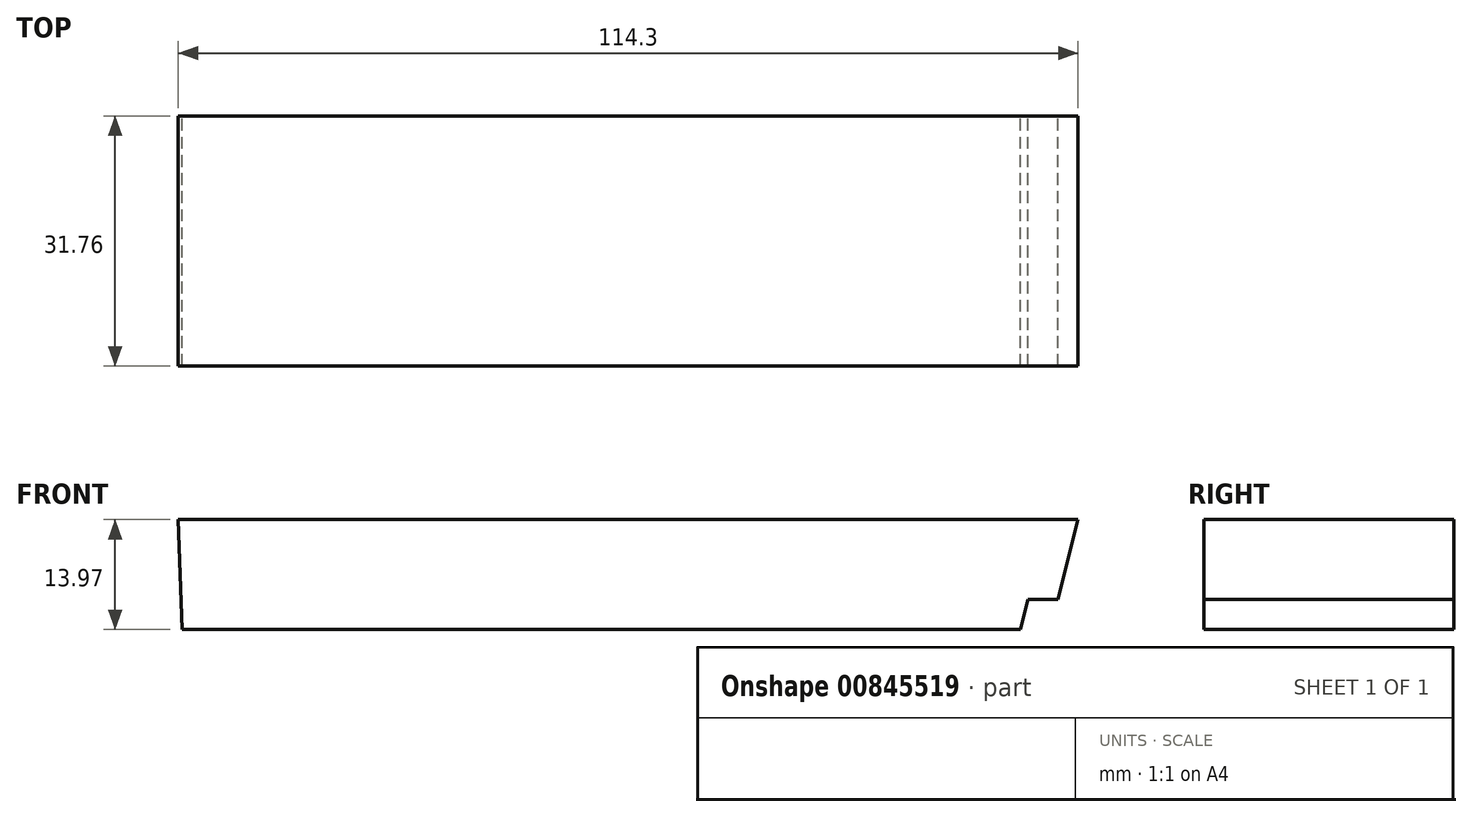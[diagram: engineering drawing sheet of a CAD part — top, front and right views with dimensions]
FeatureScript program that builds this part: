
annotation { "Feature Type Name" : "Feature", "Feature Type Description" : "" }
export const myFeature = defineFeature(function(context is Context, id is Id, definition is map)
    precondition{}
    {
        {
            var Q0;
            Q0=qCreatedBy(makeId("Front.planeOp"),FACE);
            var sketch = newSketch(context, id + "F0", { "sketchPlane" : qUnion([Q0])});
            skLineSegment(sketch, "E0", {"start": v(0, 0) * mm, "end": v(106.5, 0) * mm});
            skLineSegment(sketch, "E1", {"start": v(106.5, 0) * mm, "end": v(107.45, 3.81) * mm});
            skLineSegment(sketch, "E2", {"start": v(107.45, 3.81) * mm, "end": v(0, 0) * mm});
            skLineSegment(sketch, "E3", {"start": v(0, 0) * mm, "end": v(-0.5, 13.97) * mm});
            skLineSegment(sketch, "E4", {"start": v(-0.5, 13.97) * mm, "end": v(113.8, 13.97) * mm});
            skLineSegment(sketch, "E5", {"start": v(113.8, 13.97) * mm, "end": v(111.26, 3.81) * mm});
            skLineSegment(sketch, "E6", {"start": v(111.26, 3.81) * mm, "end": v(107.45, 3.81) * mm});
            skSolve(sketch);
        }
        {
            var Q0;
            Q0 = qSketchRegion(id + "F0", true);
            extrude(context, id + "F1", {"entities" : qUnion([Q0]), "endBound" : BoundingType.SYMMETRIC, "depth" : 31.75 * mm, "offsetDistance" : 25.4 * mm});
        }
    });
